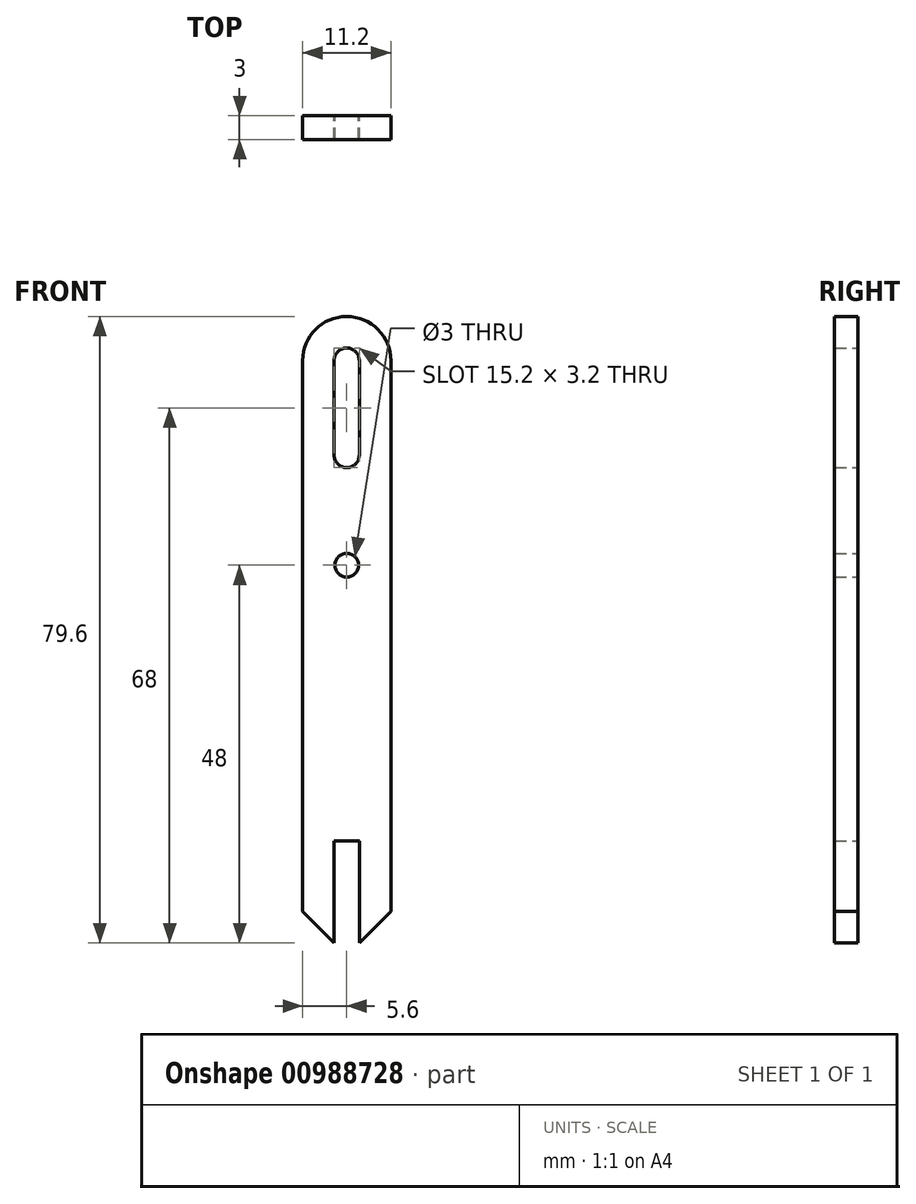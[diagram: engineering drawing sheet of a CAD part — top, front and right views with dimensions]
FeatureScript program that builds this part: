
annotation { "Feature Type Name" : "Feature", "Feature Type Description" : "" }
export const myFeature = defineFeature(function(context is Context, id is Id, definition is map)
    precondition{}
    {
        {
            var Q0;
            Q0=qCreatedBy(makeId("Front.planeOp"),FACE);
            var sketch = newSketch(context, id + "F0", { "sketchPlane" : qUnion([Q0])});
            skLineSegment(sketch, "E0", {"start": v(-1.6, 0) * mm, "end": v(-1.6, 12) * mm});
            skLineSegment(sketch, "E1", {"start": v(1.6, 12) * mm, "end": v(1.6, 0) * mm});
            skArc(sketch, "E2", {"start": v(1.6, 12) * mm, "mid": v(0, 13.6) * mm, "end": v(-1.6, 12) * mm});
            skArc(sketch, "E3", {"start": v(-1.6, 0) * mm, "mid": v(0, -1.6) * mm, "end": v(1.6, 0) * mm});
            skArc(sketch, "E4", {"start": v(5.6, 12) * mm, "mid": v(0, 17.6) * mm, "end": v(-5.6, 12) * mm});
            skLineSegment(sketch, "E5", {"start": v(-5.6, 12) * mm, "end": v(-5.6, -62) * mm});
            skLineSegment(sketch, "E6", {"start": v(5.6, 12) * mm, "end": v(5.6, -62) * mm});
            skCircle(sketch, "E7", {"center": v(0, -14) * mm, "radius": 1.5 * mm});
            skLineSegment(sketch, "E8", {"start": v(-5.6, -62) * mm, "end": v(-1.6, -62) * mm});
            skLineSegment(sketch, "E9", {"start": v(-1.6, -62) * mm, "end": v(-1.6, -49) * mm});
            skLineSegment(sketch, "E10", {"start": v(-1.6, -49) * mm, "end": v(1.6, -49) * mm});
            skLineSegment(sketch, "E11", {"start": v(1.6, -49) * mm, "end": v(1.6, -62) * mm});
            skLineSegment(sketch, "E12", {"start": v(1.6, -62) * mm, "end": v(5.6, -62) * mm});
            skLineSegment(sketch, "E13", {"start": v(0, -49) * mm, "end": v(0, -14) * mm, "construction": true});
            skSolve(sketch);
        }
        {
            var Q0;
            Q0=makeQuery(id+"F0.imprint","IMPRINT",FACE,{"disambiguationData":[TD([[makeQuery(id+"F0.imprint","IMPRINT",EDGE,{"derivedFrom":sQuery(id+"F0.wireOp",EDGE,"E0")}),1.0]])]});
            extrude(context, id + "F1", {"entities" : qUnion([Q0]), "depth" : 3 * mm, "offsetDistance" : 25 * mm});
        }
        {
            var Q0;
            Q0=makeQuery(id+"F1.opExtrude","SWEPT_EDGE",EDGE,{"disambiguationData":[OSD([sQuery(id+"F0.wireOp",EDGE,"E6"),sQuery(id+"F0.wireOp",EDGE,"E12")])]});
            var Q1;
            Q1=makeQuery(id+"F1.opExtrude","SWEPT_EDGE",EDGE,{"disambiguationData":[OSD([sQuery(id+"F0.wireOp",EDGE,"E5"),sQuery(id+"F0.wireOp",EDGE,"E8")])]});
            chamfer(context, id + "F2", {"entities" : qUnion([Q0, Q1]), "width" : 4 * mm, "tangentPropagation" : true});
        }
    });
